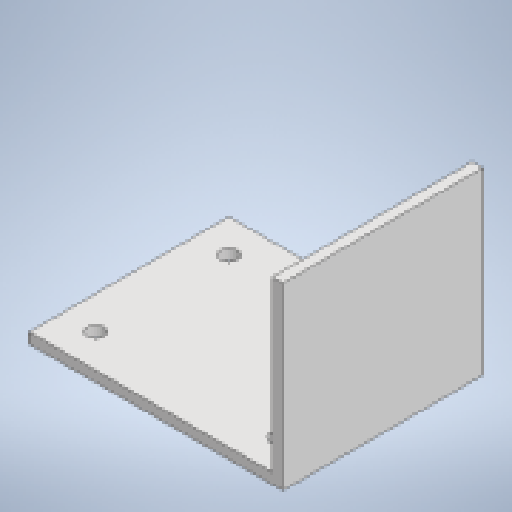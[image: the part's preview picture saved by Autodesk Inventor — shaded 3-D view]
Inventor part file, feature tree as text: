
AUTODESK INVENTOR PART (.ipt)
format: ipt  version: 2023 (Build 270158000, 158)  size: 141,312 bytes
history: native  units: mm
features: extrude x2, sketch x2
ambient origin geometry x8: Origin, YZ Plane, XZ Plane, XY Plane, X Axis, Y Axis, Z Axis, Center Point
bodies: Solid1 (feature_tree)
feature tree (4):
  extrude  "Extrusion1"  Depth=50.8mm
  extrude  "Extrusion2"  Depth=60.0mm TaperAngle=0.0deg
  sketch  "Sketch1"  dims[d0=76.2mm d1=50.8mm]
  sketch  "Sketch2"  dims[d2=3.175mm d3=60.0mm d4=0.0mm d5=12.22mm d6=53.0mm d7=40.0mm d8=5.0mm d9=60.0mm d10=0.0mm]
